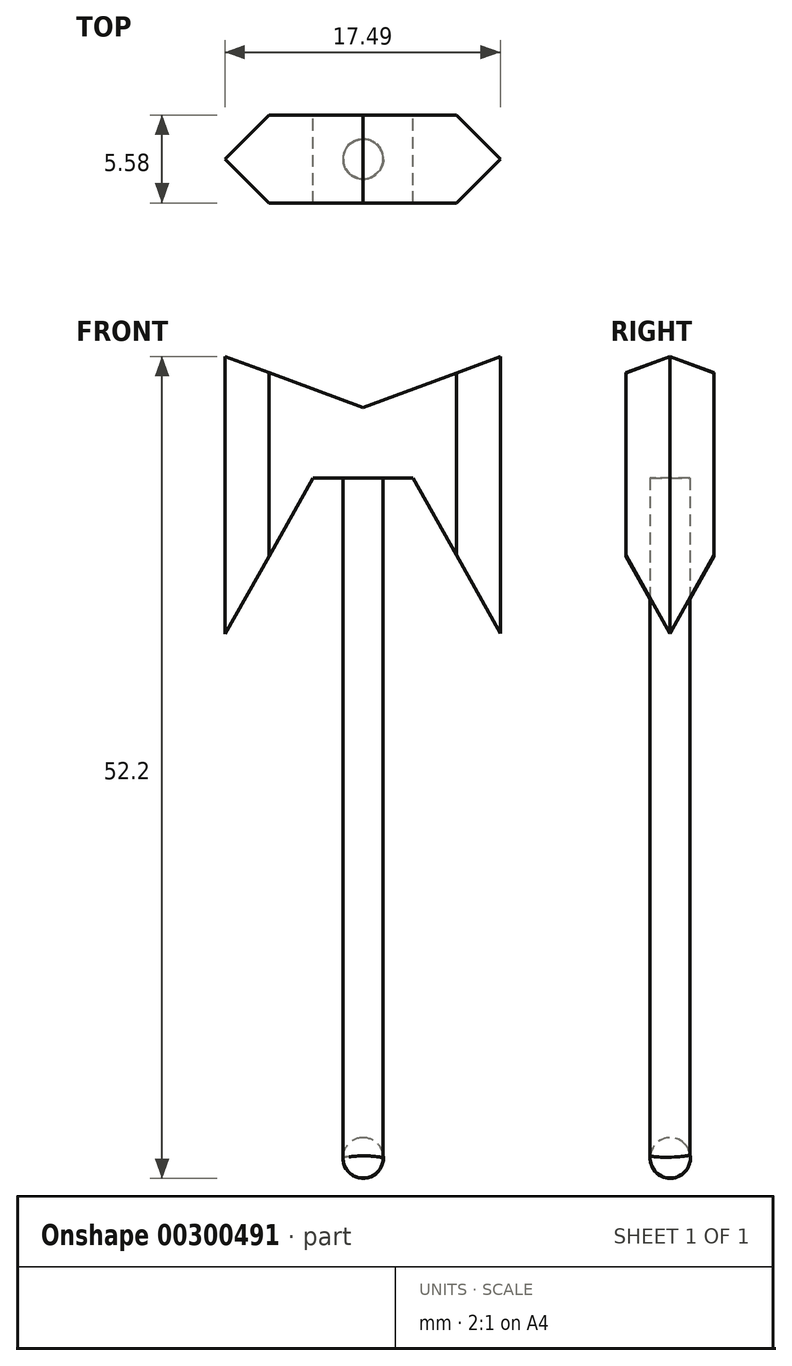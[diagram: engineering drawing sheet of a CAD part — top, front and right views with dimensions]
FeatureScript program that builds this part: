
annotation { "Feature Type Name" : "Feature", "Feature Type Description" : "" }
export const myFeature = defineFeature(function(context is Context, id is Id, definition is map)
    precondition{}
    {
        {
            var Q0;
            Q0=qCreatedBy(makeId("Top.planeOp"),FACE);
            var sketch = newSketch(context, id + "F0", { "sketchPlane" : qUnion([Q0])});
            skCircle(sketch, "E0", {"center": v(0, 0) * mm, "radius": 1.27 * mm});
            skSolve(sketch);
        }
        {
            var Q0;
            Q0 = qSketchRegion(id + "F0", true);
            extrude(context, id + "F1", {"entities" : qUnion([Q0]), "depth" : 43.18 * mm});
        }
        {
            var Q0;
            Q0=qCreatedBy(makeId("Front.planeOp"),FACE);
            var sketch = newSketch(context, id + "F2", { "sketchPlane" : qUnion([Q0])});
            skLineSegment(sketch, "E1", {"start": v(3.17, 43.18) * mm, "end": v(11, 29.24) * mm});
            skLineSegment(sketch, "E2", {"start": v(11, 29.24) * mm, "end": v(11, 51.75) * mm});
            skLineSegment(sketch, "E3", {"start": v(11, 51.75) * mm, "end": v(0, 47.67) * mm});
            skLineSegment(sketch, "E4", {"start": v(0, 47.67) * mm, "end": v(-11.06, 51.75) * mm});
            skLineSegment(sketch, "E5", {"start": v(-11.06, 51.75) * mm, "end": v(-11.06, 29.24) * mm});
            skLineSegment(sketch, "E6", {"start": v(-11.06, 29.24) * mm, "end": v(-3.17, 43.18) * mm});
            skLineSegment(sketch, "E7", {"start": v(3.17, 43.18) * mm, "end": v(-3.17, 43.18) * mm});
            skSolve(sketch);
        }
        {
            var Q0;
            Q0=makeQuery(id+"F2.imprint","IMPRINT",FACE,{"disambiguationData":[TD([[makeQuery(id+"F2.imprint","IMPRINT",EDGE,{"derivedFrom":sQuery(id+"F2.wireOp",EDGE,"E1")}),1.0]])]});
            extrude(context, id + "F3", {"entities" : qUnion([Q0]), "endBound" : BoundingType.SYMMETRIC, "depth" : 5.6 * mm});
        }
        {
            var Q0;
            Q0=makeQuery(id+"F3.opExtrude","CAP_EDGE",EDGE,{"disambiguationData":[OSD([sQuery(id+"F2.wireOp",EDGE,"E2")])],"isStart":false});
            var Q1;
            Q1=makeQuery(id+"F3.opExtrude","CAP_EDGE",EDGE,{"disambiguationData":[OSD([sQuery(id+"F2.wireOp",EDGE,"E2")])],"isStart":true});
            var Q2;
            Q2=makeQuery(id+"F3.opExtrude","CAP_EDGE",EDGE,{"disambiguationData":[OSD([sQuery(id+"F2.wireOp",EDGE,"E5")])],"isStart":false});
            var Q3;
            Q3=makeQuery(id+"F3.opExtrude","CAP_EDGE",EDGE,{"disambiguationData":[OSD([sQuery(id+"F2.wireOp",EDGE,"E5")])],"isStart":true});
            chamfer(context, id + "F4", {"entities" : qUnion([Q0, Q1, Q2, Q3]), "width" : 5.08 * mm, "tangentPropagation" : true});
        }
        {
            var Q0;
            Q0=qCreatedBy(makeId("Top.planeOp"),FACE);
            var sketch = newSketch(context, id + "F5", { "sketchPlane" : qUnion([Q0])});
            skArc(sketch, "E8", {"start": v(0, 1.28) * mm, "mid": v(-1.27, 0) * mm, "end": v(0, -1.28) * mm});
            skLineSegment(sketch, "E9", {"start": v(0, -1.28) * mm, "end": v(0, 1.28) * mm});
            skSolve(sketch);
        }
        {
            var Q0;
            Q0 = qSketchRegion(id + "F5", true);
            var Q1;
            Q1=sQuery(id+"F5.wireOp",EDGE,"E9");
            revolve(context, id + "F6", {"operationType" : NewBodyOperationType.ADD, "entities" : qUnion([Q0]), "axis" : qUnion([Q1]), "revolveType" : RevolveType.FULL});
        }
    });
